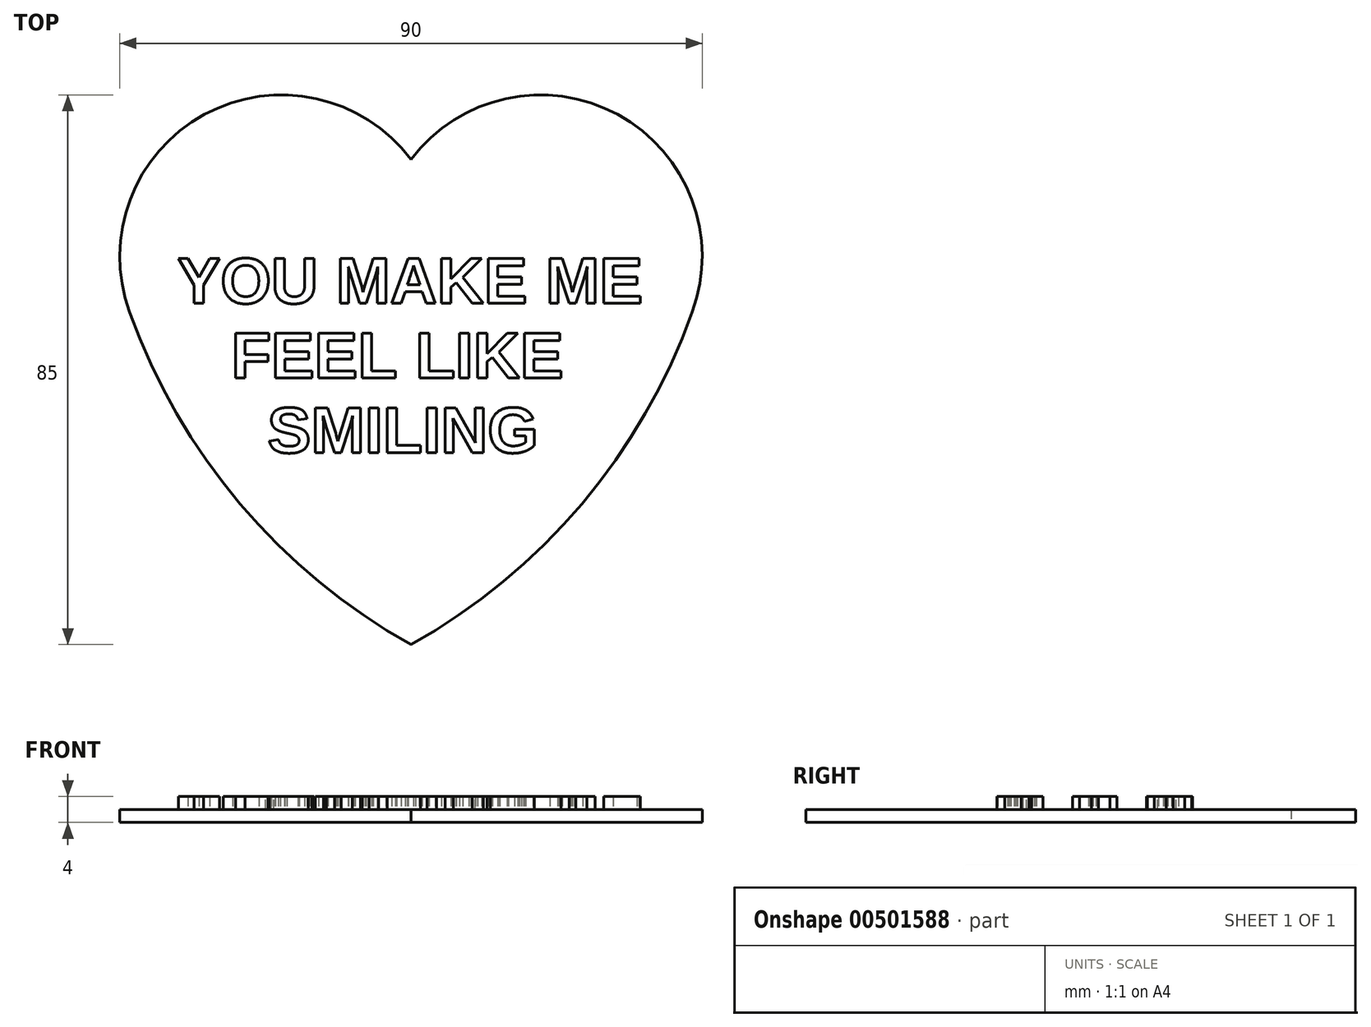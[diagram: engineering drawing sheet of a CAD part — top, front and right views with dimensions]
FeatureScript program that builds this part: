
annotation { "Feature Type Name" : "Feature", "Feature Type Description" : "" }
export const myFeature = defineFeature(function(context is Context, id is Id, definition is map)
    precondition{}
    {
        {
            var Q0;
            Q0=qCreatedBy(makeId("Top.planeOp"),FACE);
            var sketch = newSketch(context, id + "F0", { "sketchPlane" : qUnion([Q0])});
            skArc(sketch, "E0", {"start": v(-43.47, 1.39) * mm, "mid": v(-26.4, -28.25) * mm, "end": v(0, -50) * mm});
            skArc(sketch, "E1", {"start": v(0, 25) * mm, "mid": v(-31.93, 31.97) * mm, "end": v(-43.47, 1.39) * mm});
            skArc(sketch, "E2.MirrorCS", {"start": v(0, 25) * mm, "mid": v(31.93, 31.97) * mm, "end": v(43.47, 1.39) * mm});
            skArc(sketch, "E3.MirrorCS", {"start": v(43.47, 1.39) * mm, "mid": v(26.4, -28.25) * mm, "end": v(0, -50) * mm});
            skSolve(sketch);
        }
        {
            var Q0;
            Q0=qSketchRegion(id+"F0",true);
            extrude(context, id + "F1", {"entities" : qUnion([Q0]), "depth" : 2 * mm});
        }
        {
            var Q0;
            Q0=makeQuery(id+"F1.opExtrude","CAP_FACE",FACE,{"disambiguationData":[OSD([sQuery(id+"F0.wireOp",EDGE,"E0"),sQuery(id+"F0.wireOp",EDGE,"E1"),sQuery(id+"F0.wireOp",EDGE,"E2.MirrorCS"),sQuery(id+"F0.wireOp",EDGE,"E3.MirrorCS")])],"isStart":false});
            var sketch = newSketch(context, id + "F2", { "sketchPlane" : qUnion([Q0])});
            skText(sketch, "E4", { "text": "YOU MAKE ME   \n   FEEL LIKE \n     SMILING", "fontName": "Arimo-Bold.ttf"});
            const initialGuessF2  = {"E4": [-0.03613, 0.00277, 1, 0, 0.00723]};
            skSetInitialGuess(sketch, initialGuessF2);
            skSolve(sketch);
        }
        {
            var Q0;
            Q0=qSketchRegion(id+"F2",true);
            extrude(context, id + "F3", {"entities" : qUnion([Q0]), "operationType" : NewBodyOperationType.ADD, "depth" : 2 * mm});
        }
    });
